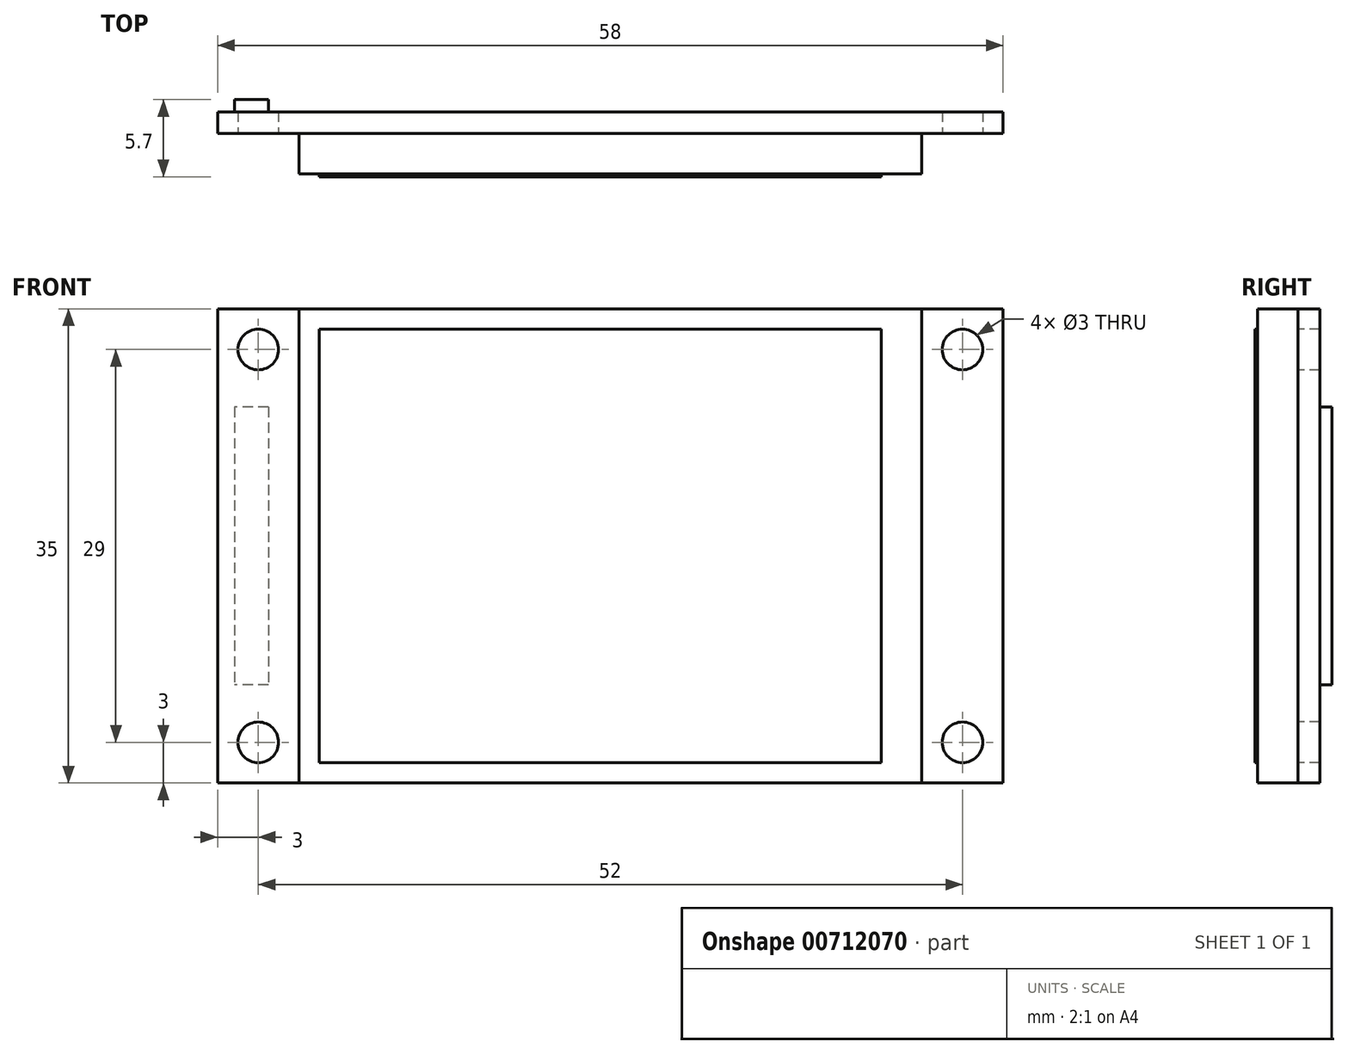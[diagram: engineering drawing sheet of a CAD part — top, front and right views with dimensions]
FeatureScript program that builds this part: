
annotation { "Feature Type Name" : "Feature", "Feature Type Description" : "" }
export const myFeature = defineFeature(function(context is Context, id is Id, definition is map)
    precondition{}
    {
        {
            var Q0;
            Q0=qCreatedBy(makeId("Front.planeOp"),FACE);
            var sketch = newSketch(context, id + "F0", { "sketchPlane" : qUnion([Q0])});
            skLineSegment(sketch, "E0.bottom", {"start": v(-29, 17.5) * mm, "end": v(29, 17.5) * mm});
            skLineSegment(sketch, "E0.top", {"start": v(-29, -17.5) * mm, "end": v(29, -17.5) * mm});
            skLineSegment(sketch, "E0.left", {"start": v(-29, 17.5) * mm, "end": v(-29, -17.5) * mm});
            skLineSegment(sketch, "E0.right", {"start": v(29, 17.5) * mm, "end": v(29, -17.5) * mm});
            skPoint(sketch, "E0.middle", {"position": v(0, 0) * mm});
            skCircle(sketch, "E1", {"center": v(-26, 14.5) * mm, "radius": 1.5 * mm});
            skCircle(sketch, "E2", {"center": v(26, 14.5) * mm, "radius": 1.5 * mm});
            skCircle(sketch, "E3", {"center": v(-26, -14.5) * mm, "radius": 1.5 * mm});
            skCircle(sketch, "E4", {"center": v(26, -14.5) * mm, "radius": 1.5 * mm});
            skLineSegment(sketch, "E5.0", {"start": v(23, 17.5) * mm, "end": v(23, -17.5) * mm});
            skLineSegment(sketch, "E6.0", {"start": v(-23, 17.5) * mm, "end": v(-23, -17.5) * mm});
            skLineSegment(sketch, "E7", {"start": v(-29, 0) * mm, "end": v(-26.5, 0) * mm, "construction": true});
            skLineSegment(sketch, "E8.bottom", {"start": v(-25.25, 10.25) * mm, "end": v(-27.75, 10.25) * mm});
            skLineSegment(sketch, "E8.top", {"start": v(-25.25, -10.25) * mm, "end": v(-27.75, -10.25) * mm});
            skLineSegment(sketch, "E8.left", {"start": v(-25.25, 10.25) * mm, "end": v(-25.25, -10.25) * mm});
            skLineSegment(sketch, "E8.right", {"start": v(-27.75, 10.25) * mm, "end": v(-27.75, -10.25) * mm});
            skPoint(sketch, "E8.middle", {"position": v(-26.5, 0) * mm});
            skSolve(sketch);
        }
        {
            var Q0;
            {var subQ0=sQuery(id+"F0.wireOp",EDGE,"E5.0");Q0=makeQuery(id+"F0.imprint","IMPRINT",FACE,{"disambiguationData":[TD([[makeQuery(id+"F0.imprint","IMPRINT",EDGE,{"derivedFrom":subQ0}),-1.0]])]});}
            var Q1;
            {var subQ0=sQuery(id+"F0.wireOp",EDGE,"E0.right");Q1=makeQuery(id+"F0.imprint","IMPRINT",FACE,{"disambiguationData":[TD([[makeQuery(id+"F0.imprint","IMPRINT",EDGE,{"derivedFrom":subQ0}),-1.0]])]});}
            var Q2;
            {var subQ0=sQuery(id+"F0.wireOp",EDGE,"E0.left");Q2=makeQuery(id+"F0.imprint","IMPRINT",FACE,{"disambiguationData":[TD([[makeQuery(id+"F0.imprint","IMPRINT",EDGE,{"derivedFrom":subQ0}),1.0]])]});}
            extrude(context, id + "F1", {"entities" : qUnion([Q0, Q1, Q2]), "oppositeDirection" : true, "depth" : 1.6 * mm, "offsetDistance" : 25 * mm});
        }
        {
            var Q0;
            {var subQ0=sQuery(id+"F0.wireOp",EDGE,"E5.0");Q0=makeQuery(id+"F0.imprint","IMPRINT",FACE,{"disambiguationData":[TD([[makeQuery(id+"F0.imprint","IMPRINT",EDGE,{"derivedFrom":subQ0}),-1.0]])]});}
            extrude(context, id + "F2", {"entities" : qUnion([Q0]), "depth" : 3 * mm, "offsetDistance" : 25 * mm});
        }
        {
            var Q0;
            Q0=makeQuery(id+"F0.imprint","IMPRINT",FACE,{"disambiguationData":[TD([[makeQuery(id+"F0.imprint","IMPRINT",EDGE,{"derivedFrom":sQuery(id+"F0.wireOp",EDGE,"E8.bottom")}),1.0]])]});
            extrude(context, id + "F3", {"entities" : qUnion([Q0]), "operationType" : NewBodyOperationType.ADD, "oppositeDirection" : true, "depth" : 2.5 * mm, "offsetDistance" : 25 * mm});
        }
        {
            var Q0;
            Q0=makeQuery(id+"F2.opExtrude","CAP_FACE",FACE,{"disambiguationData":[OSD([sQuery(id+"F0.wireOp",EDGE,"E0.bottom"),sQuery(id+"F0.wireOp",EDGE,"E0.top"),sQuery(id+"F0.wireOp",EDGE,"E5.0"),sQuery(id+"F0.wireOp",EDGE,"E6.0")])],"isStart":false});
            var sketch = newSketch(context, id + "F4", { "sketchPlane" : qUnion([Q0])});
            skLineSegment(sketch, "E9.0", {"start": v(-21.5, -16) * mm, "end": v(20, -16) * mm});
            skLineSegment(sketch, "E9.1", {"start": v(-21.5, 16) * mm, "end": v(-21.5, -16) * mm});
            skLineSegment(sketch, "E9.2", {"start": v(-21.5, 16) * mm, "end": v(20, 16) * mm});
            skLineSegment(sketch, "E10", {"start": v(20, 16) * mm, "end": v(20, -16) * mm});
            skSolve(sketch);
        }
        {
            var Q0;
            Q0=makeQuery(id+"F4.imprint","IMPRINT",FACE,{"disambiguationData":[TD([[makeQuery(id+"F4.imprint","IMPRINT",EDGE,{"derivedFrom":sQuery(id+"F4.wireOp",EDGE,"E9.0")}),1.0]])]});
            extrude(context, id + "F5", {"entities" : qUnion([Q0]), "depth" : 0.2 * mm, "offsetDistance" : 25 * mm});
        }
    });
